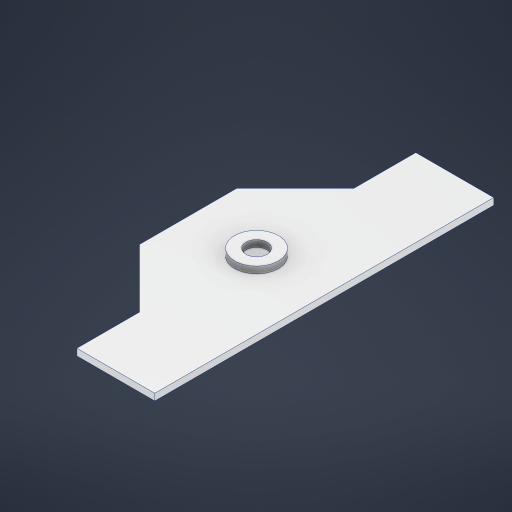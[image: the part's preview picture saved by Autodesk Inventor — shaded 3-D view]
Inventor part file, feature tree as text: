
AUTODESK INVENTOR PART (.ipt)
format: ipt  version: 2024 (Build 280153000, 153)  size: 194,560 bytes
history: native  units: mm
features: extrude x2, sketch x2
ambient origin geometry x8: Origin, YZ Plane, XZ Plane, XY Plane, X Axis, Y Axis, Z Axis, Center Point
bodies: Solid1 (feature_tree)
feature tree (4):
  extrude  "Extrusion1"  Depth=117.0mm
  extrude  "Extrusion2"  Depth=10.0mm
  sketch  "Sketch1"  dims[d0=509.0mm d1=117.0mm]
  sketch  "Sketch2"  dims[d2=117.0mm d3=93.0mm d4=94.0mm d6=88.0mm d7=88.0mm d8=88.0mm d9=88.0mm d10=10.0mm d11=0.0mm d12=10.0mm d13=0.0mm]
